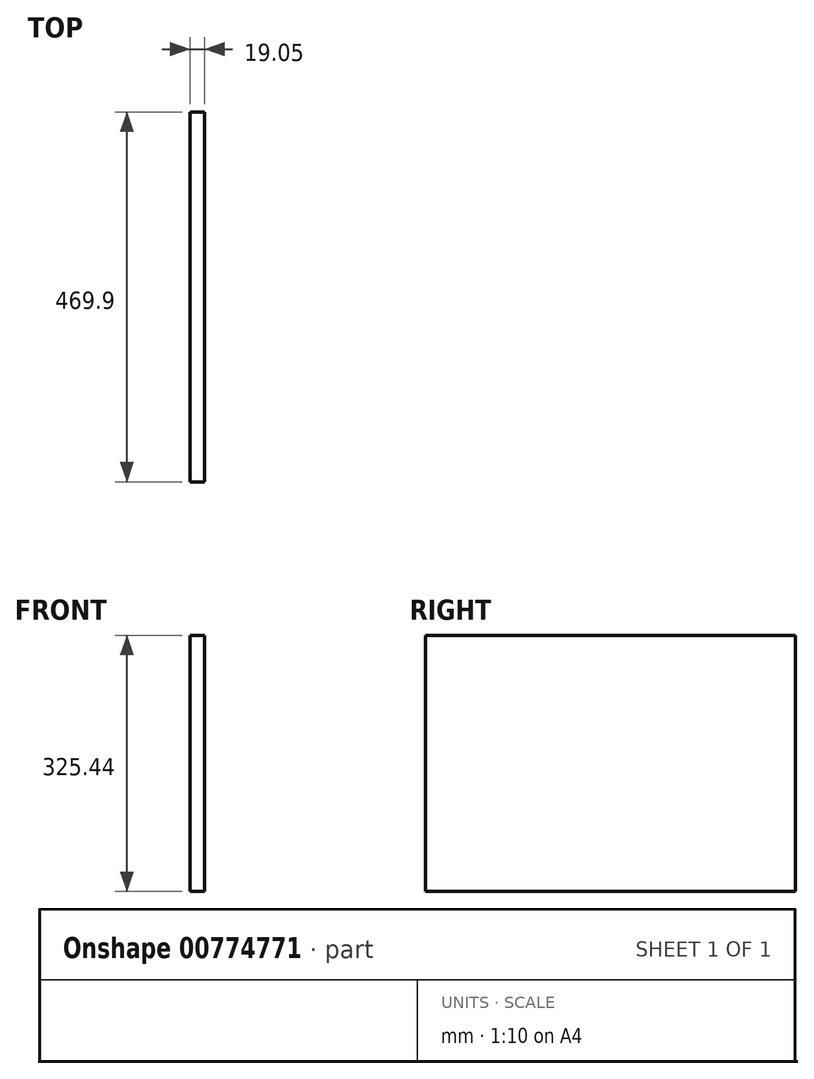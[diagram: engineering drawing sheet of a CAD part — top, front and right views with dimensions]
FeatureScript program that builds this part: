
annotation { "Feature Type Name" : "Feature", "Feature Type Description" : "" }
export const myFeature = defineFeature(function(context is Context, id is Id, definition is map)
    precondition{}
    {
        {
            var Q0;
            Q0=qCreatedBy(makeId("Front.planeOp"),FACE);
            var sketch = newSketch(context, id + "F0", { "sketchPlane" : qUnion([Q0])});
            skLineSegment(sketch, "E0.bottom", {"start": v(0, 0) * mm, "end": v(-19.05, 0) * mm});
            skLineSegment(sketch, "E0.top", {"start": v(0, 325.44) * mm, "end": v(-19.05, 325.44) * mm});
            skLineSegment(sketch, "E0.left", {"start": v(0, 0) * mm, "end": v(0, 325.44) * mm});
            skLineSegment(sketch, "E0.right", {"start": v(-19.05, 0) * mm, "end": v(-19.05, 325.44) * mm});
            skSolve(sketch);
        }
        {
            var Q0;
            Q0 = qSketchRegion(id + "F0", true);
            extrude(context, id + "F1", {"entities" : qUnion([Q0]), "depth" : 469.9 * mm, "offsetDistance" : 25.4 * mm});
        }
    });
